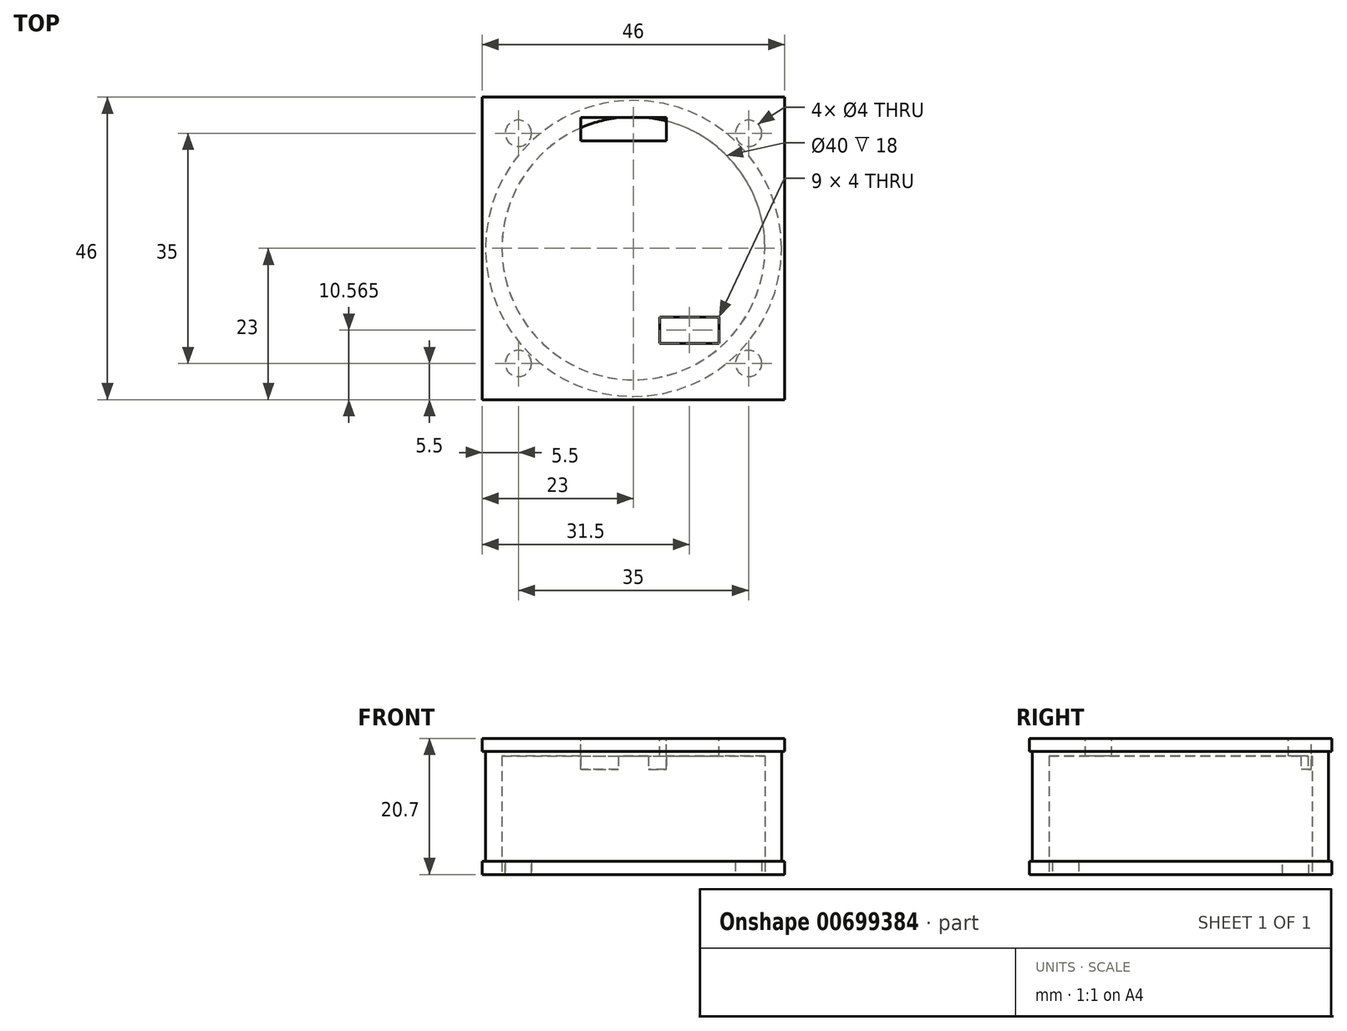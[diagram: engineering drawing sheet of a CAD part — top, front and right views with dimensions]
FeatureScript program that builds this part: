
annotation { "Feature Type Name" : "Feature", "Feature Type Description" : "" }
export const myFeature = defineFeature(function(context is Context, id is Id, definition is map)
    precondition{}
    {
        {
            var Q0;
            Q0=qCreatedBy(makeId("Top.planeOp"),FACE);
            var sketch = newSketch(context, id + "F0", { "sketchPlane" : qUnion([Q0])});
            skLineSegment(sketch, "E0.bottom", {"start": v(0, 0) * mm, "end": v(46, 0) * mm});
            skLineSegment(sketch, "E0.top", {"start": v(0, -46) * mm, "end": v(46, -46) * mm});
            skLineSegment(sketch, "E0.left", {"start": v(0, 0) * mm, "end": v(0, -46) * mm});
            skLineSegment(sketch, "E0.right", {"start": v(46, 0) * mm, "end": v(46, -46) * mm});
            skSolve(sketch);
        }
        {
            var Q0;
            Q0=makeQuery(id+"F0.imprint","IMPRINT",FACE,{"disambiguationData":[TD([[makeQuery(id+"F0.imprint","IMPRINT",EDGE,{"derivedFrom":sQuery(id+"F0.wireOp",EDGE,"E0.bottom")}),-1.0]])]});
            extrude(context, id + "F1", {"entities" : qUnion([Q0]), "depth" : 2 * mm, "offsetDistance" : 25.4 * mm});
        }
        {
            var Q0;
            Q0=makeQuery(id+"F1.opExtrude","CAP_FACE",FACE,{"disambiguationData":[OSD([sQuery(id+"F0.wireOp",EDGE,"E0.bottom"),sQuery(id+"F0.wireOp",EDGE,"E0.top"),sQuery(id+"F0.wireOp",EDGE,"E0.left"),sQuery(id+"F0.wireOp",EDGE,"E0.right")])],"isStart":false});
            var sketch = newSketch(context, id + "F2", { "sketchPlane" : qUnion([Q0])});
            skCircle(sketch, "E1", {"center": v(5.5, -5.5) * mm, "radius": 2 * mm});
            skSolve(sketch);
        }
        {
            var Q0;
            Q0 = qSketchRegion(id + "F2", true);
            extrude(context, id + "F3", {"entities" : qUnion([Q0]), "operationType" : NewBodyOperationType.REMOVE, "oppositeDirection" : true, "depth" : 25.4 * mm, "offsetDistance" : 25.4 * mm});
        }
        {
            var Q0;
            Q0=makeQuery(id+"F1.opExtrude","CAP_FACE",FACE,{"disambiguationData":[OSD([sQuery(id+"F0.wireOp",EDGE,"E0.bottom"),sQuery(id+"F0.wireOp",EDGE,"E0.top"),sQuery(id+"F0.wireOp",EDGE,"E0.left"),sQuery(id+"F0.wireOp",EDGE,"E0.right")])],"isStart":true});
            var sketch = newSketch(context, id + "F4", { "sketchPlane" : qUnion([Q0])});
            skCircle(sketch, "E2", {"center": v(23, 23) * mm, "radius": 22.5 * mm});
            skSolve(sketch);
        }
        {
            var Q0;
            Q0=makeQuery(id+"F4.imprint","IMPRINT",FACE,{"disambiguationData":[TD([[makeQuery(id+"F4.imprint","IMPRINT",EDGE,{"derivedFrom":sQuery(id+"F4.wireOp",EDGE,"E2")}),1.0]])]});
            var Q1;
            Q1=sQuery(id+"F4.wireOp",EDGE,"E2");
            extrude(context, id + "F5", {"entities" : qUnion([Q0]), "operationType" : NewBodyOperationType.ADD, "surfaceEntities" : qUnion([Q1]), "oppositeDirection" : true, "depth" : 20 * mm, "offsetDistance" : 25.4 * mm});
        }
        {
            var Q0;
            Q0=makeQuery(id+"F1.opExtrude","CAP_FACE",FACE,{"disambiguationData":[OSD([sQuery(id+"F0.wireOp",EDGE,"E0.bottom"),sQuery(id+"F0.wireOp",EDGE,"E0.top"),sQuery(id+"F0.wireOp",EDGE,"E0.left"),sQuery(id+"F0.wireOp",EDGE,"E0.right")])],"isStart":false});
            var sketch = newSketch(context, id + "F6", { "sketchPlane" : qUnion([Q0])});
            skCircle(sketch, "E3", {"center": v(23, -23) * mm, "radius": 20 * mm});
            skSolve(sketch);
        }
        {
            var Q0;
            Q0 = qSketchRegion(id + "F6", true);
            extrude(context, id + "F7", {"entities" : qUnion([Q0]), "operationType" : NewBodyOperationType.REMOVE, "endBound" : BoundingType.SYMMETRIC, "depth" : 32 * mm, "offsetDistance" : 25.4 * mm});
        }
        {
            var Q0;
            Q0=makeQuery(id+"F5.opExtrude","CAP_FACE",FACE,{"disambiguationData":[OSD([sQuery(id+"F4.wireOp",EDGE,"E2")])],"isStart":false});
            cPlane(context, id + "F8", {"entities" : qUnion([Q0]), "cplaneType" : CPlaneType.OFFSET, "offset" : 1.3 * mm, "oppositeDirection" : true, "width" : 150 * mm, "height" : 150 * mm});
        }
        {
            var Q0;
            Q0=qCreatedBy(id+"F8.planeOp",FACE);
            var sketch = newSketch(context, id + "F9", { "sketchPlane" : qUnion([Q0])});
            skLineSegment(sketch, "E4.bottom", {"start": v(46, 0) * mm, "end": v(0, 0) * mm});
            skLineSegment(sketch, "E4.top", {"start": v(46, -46) * mm, "end": v(0, -46) * mm});
            skLineSegment(sketch, "E4.left", {"start": v(46, 0) * mm, "end": v(46, -46) * mm});
            skLineSegment(sketch, "E4.right", {"start": v(0, 0) * mm, "end": v(0, -46) * mm});
            skSolve(sketch);
        }
        {
            var Q0;
            Q0 = qSketchRegion(id + "F9", true);
            extrude(context, id + "F10", {"entities" : qUnion([Q0]), "operationType" : NewBodyOperationType.ADD, "depth" : 2 * mm, "offsetDistance" : 25 * mm});
        }
        {
            var Q0;
            Q0=makeQuery(id+"F10.opExtrude","CAP_FACE",FACE,{"disambiguationData":[OSD([sQuery(id+"F9.wireOp",EDGE,"E4.bottom"),sQuery(id+"F9.wireOp",EDGE,"E4.top"),sQuery(id+"F9.wireOp",EDGE,"E4.left"),sQuery(id+"F9.wireOp",EDGE,"E4.right")])],"isStart":false});
            var sketch = newSketch(context, id + "F11", { "sketchPlane" : qUnion([Q0])});
            skSolve(sketch);
        }
        {
            var Q0;
            Q0=makeQuery(id+"F11.imprint","IMPRINT",FACE,{"disambiguationData":[TD([[makeQuery(id+"F11.imprint","IMPRINT",EDGE,{"derivedFrom":makeQuery(id+"F10.opExtrude","CAP_EDGE",EDGE,{"disambiguationData":[OSD([sQuery(id+"F9.wireOp",EDGE,"E4.bottom")])],"isStart":false})}),1.0]])]});
            var sketch = newSketch(context, id + "F12", { "sketchPlane" : qUnion([Q0])});
            skLineSegment(sketch, "E5.bottom", {"start": v(15, -3.13) * mm, "end": v(28, -3.13) * mm});
            skLineSegment(sketch, "E5.top", {"start": v(15, -6.63) * mm, "end": v(28, -6.63) * mm});
            skLineSegment(sketch, "E5.left", {"start": v(15, -3.13) * mm, "end": v(15, -6.63) * mm});
            skLineSegment(sketch, "E5.right", {"start": v(28, -3.13) * mm, "end": v(28, -6.63) * mm});
            skSolve(sketch);
        }
        {
            var Q0;
            Q0 = qSketchRegion(id + "F12", true);
            extrude(context, id + "F13", {"entities" : qUnion([Q0]), "operationType" : NewBodyOperationType.REMOVE, "oppositeDirection" : true, "depth" : 4.7 * mm, "offsetDistance" : 25 * mm});
        }
        {
            var Q0;
            Q0=makeQuery(id+"F11.imprint","IMPRINT",FACE,{"disambiguationData":[TD([[makeQuery(id+"F11.imprint","IMPRINT",EDGE,{"derivedFrom":makeQuery(id+"F10.opExtrude","CAP_EDGE",EDGE,{"disambiguationData":[OSD([sQuery(id+"F9.wireOp",EDGE,"E4.bottom")])],"isStart":false})}),1.0]])]});
            var sketch = newSketch(context, id + "F14", { "sketchPlane" : qUnion([Q0])});
            skLineSegment(sketch, "E6.bottom", {"start": v(27, -33.44) * mm, "end": v(36, -33.44) * mm});
            skLineSegment(sketch, "E6.top", {"start": v(27, -37.44) * mm, "end": v(36, -37.44) * mm});
            skLineSegment(sketch, "E6.left", {"start": v(27, -33.44) * mm, "end": v(27, -37.44) * mm});
            skLineSegment(sketch, "E6.right", {"start": v(36, -33.44) * mm, "end": v(36, -37.44) * mm});
            skSolve(sketch);
        }
        {
            var Q0;
            Q0 = qSketchRegion(id + "F14", true);
            extrude(context, id + "F15", {"entities" : qUnion([Q0]), "operationType" : NewBodyOperationType.REMOVE, "oppositeDirection" : true, "depth" : 2.7 * mm, "offsetDistance" : 25 * mm});
        }
        {
            var Q0;
            {var subQ0=sQuery(id+"F4.wireOp",EDGE,"E2");var subQ1=makeQuery(id+"F1.opExtrude","CAP_EDGE",EDGE,{"disambiguationData":[OSD([sQuery(id+"F0.wireOp",EDGE,"E0.top")])],"isStart":true});var subQ2=makeQuery(id+"F4.imprint","INTERSECT",VERTEX,{"derivedFrom":[subQ1,subQ0]});Q0=makeQuery(id+"F4.imprint","IMPRINT",FACE,{"disambiguationData":[TD([[makeQuery(id+"F4.imprint","IMPRINT",EDGE,{"disambiguationData":[TD([[subQ2,1.0]])],"derivedFrom":subQ0}),-1.0]])]});}
            var sketch = newSketch(context, id + "F16", { "sketchPlane" : qUnion([Q0])});
            skCircle(sketch, "E7", {"center": v(40.5, 40.5) * mm, "radius": 2 * mm});
            skSolve(sketch);
        }
        {
            var Q0;
            Q0 = qSketchRegion(id + "F16", true);
            extrude(context, id + "F17", {"entities" : qUnion([Q0]), "operationType" : NewBodyOperationType.REMOVE, "oppositeDirection" : true, "depth" : 2 * mm, "offsetDistance" : 25 * mm});
        }
        {
            var Q0;
            {var subQ0=sQuery(id+"F4.wireOp",EDGE,"E2");var subQ1=makeQuery(id+"F1.opExtrude","CAP_EDGE",EDGE,{"disambiguationData":[OSD([sQuery(id+"F0.wireOp",EDGE,"E0.right")])],"isStart":true});var subQ2=makeQuery(id+"F4.imprint","INTERSECT",VERTEX,{"derivedFrom":[subQ1,subQ0]});Q0=makeQuery(id+"F4.imprint","IMPRINT",FACE,{"disambiguationData":[TD([[makeQuery(id+"F4.imprint","IMPRINT",EDGE,{"disambiguationData":[TD([[subQ2,1.0]])],"derivedFrom":subQ0}),-1.0]])]});}
            var sketch = newSketch(context, id + "F18", { "sketchPlane" : qUnion([Q0])});
            skCircle(sketch, "E8", {"center": v(40.5, 5.5) * mm, "radius": 2 * mm});
            skSolve(sketch);
        }
        {
            var Q0;
            Q0 = qSketchRegion(id + "F18", true);
            extrude(context, id + "F19", {"entities" : qUnion([Q0]), "operationType" : NewBodyOperationType.REMOVE, "oppositeDirection" : true, "depth" : 2 * mm, "offsetDistance" : 25 * mm});
        }
        {
            var Q0;
            {var subQ0=sQuery(id+"F4.wireOp",EDGE,"E2");var subQ1=makeQuery(id+"F1.opExtrude","CAP_EDGE",EDGE,{"disambiguationData":[OSD([sQuery(id+"F0.wireOp",EDGE,"E0.top")])],"isStart":true});var subQ2=makeQuery(id+"F4.imprint","INTERSECT",VERTEX,{"derivedFrom":[subQ1,subQ0]});Q0=makeQuery(id+"F4.imprint","IMPRINT",FACE,{"disambiguationData":[TD([[makeQuery(id+"F4.imprint","IMPRINT",EDGE,{"disambiguationData":[TD([[subQ2,-1.0]])],"derivedFrom":subQ0}),-1.0]])]});}
            var sketch = newSketch(context, id + "F20", { "sketchPlane" : qUnion([Q0])});
            skCircle(sketch, "E9", {"center": v(5.5, 40.5) * mm, "radius": 2 * mm});
            skSolve(sketch);
        }
        {
            var Q0;
            Q0 = qSketchRegion(id + "F20", true);
            extrude(context, id + "F21", {"entities" : qUnion([Q0]), "operationType" : NewBodyOperationType.REMOVE, "oppositeDirection" : true, "depth" : 2 * mm, "offsetDistance" : 25 * mm});
        }
    });
